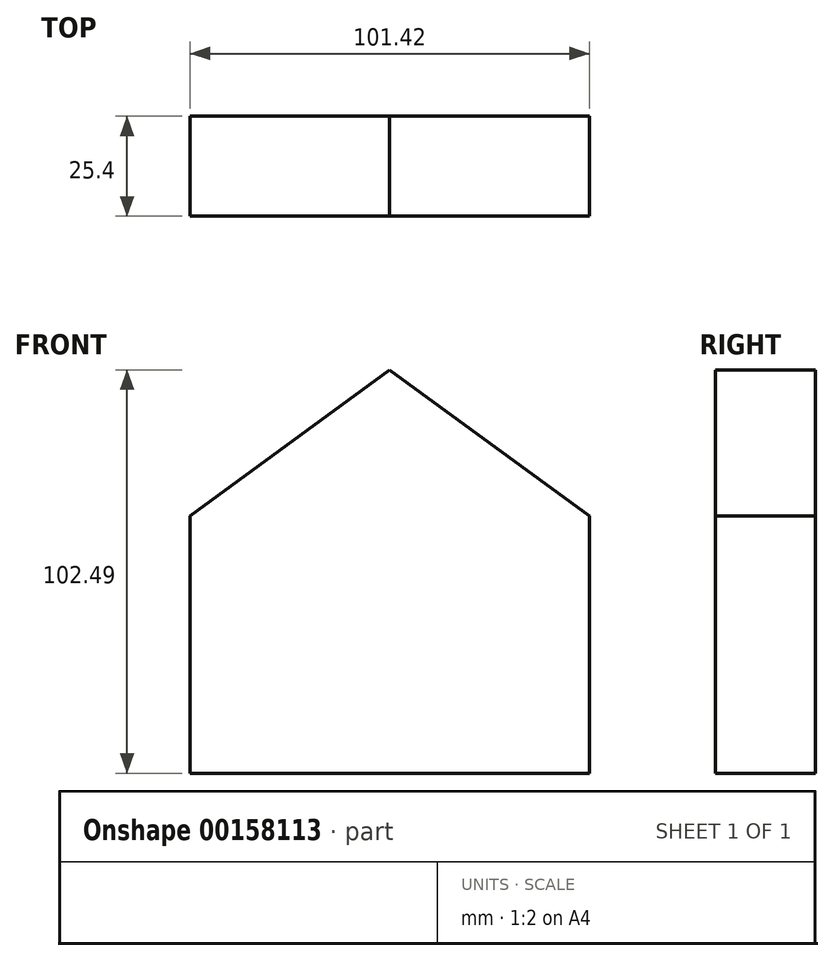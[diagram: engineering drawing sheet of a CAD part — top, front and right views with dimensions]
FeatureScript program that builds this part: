
annotation { "Feature Type Name" : "Feature", "Feature Type Description" : "" }
export const myFeature = defineFeature(function(context is Context, id is Id, definition is map)
    precondition{}
    {
        {
            var Q0;
            Q0=qCreatedBy(makeId("Front.planeOp"),FACE);
            var sketch = newSketch(context, id + "F0", { "sketchPlane" : qUnion([Q0])});
            skLineSegment(sketch, "E0.bottom", {"start": v(50.7, 32.65) * mm, "end": v(-50.7, 32.65) * mm});
            skLineSegment(sketch, "E0.top", {"start": v(50.7, -32.65) * mm, "end": v(-50.7, -32.65) * mm});
            skLineSegment(sketch, "E0.left", {"start": v(50.7, 32.65) * mm, "end": v(50.7, -32.65) * mm});
            skLineSegment(sketch, "E0.right", {"start": v(-50.7, 32.65) * mm, "end": v(-50.7, -32.65) * mm});
            skPoint(sketch, "E0.middle", {"position": v(0, 0) * mm});
            skPoint(sketch, "E1.endSnap0", {"position": v(0, 32.65) * mm});
            skLineSegment(sketch, "E2", {"start": v(0, 69.84) * mm, "end": v(50.7, 32.65) * mm});
            skLineSegment(sketch, "E3", {"start": v(0, 69.84) * mm, "end": v(-50.7, 32.65) * mm});
            skSolve(sketch);
        }
        {
            var Q0;
            Q0=makeQuery(id+"F0.imprint","IMPRINT",FACE,{"disambiguationData":[TD([[makeQuery(id+"F0.imprint","IMPRINT",EDGE,{"derivedFrom":sQuery(id+"F0.wireOp",EDGE,"E0.bottom")}),1.0]])]});
            var Q1;
            Q1=makeQuery(id+"F0.imprint","IMPRINT",FACE,{"disambiguationData":[TD([[makeQuery(id+"F0.imprint","IMPRINT",EDGE,{"derivedFrom":sQuery(id+"F0.wireOp",EDGE,"E0.bottom")}),-1.0]])]});
            extrude(context, id + "F1", {"entities" : qUnion([Q0, Q1]), "depth" : 25.4 * mm});
        }
    });
